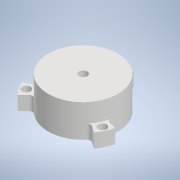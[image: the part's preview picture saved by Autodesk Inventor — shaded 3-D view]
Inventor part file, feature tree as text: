
AUTODESK INVENTOR PART (.ipt)
format: ipt  version: 2022 (Build 260153000, 153)  size: 250,368 bytes
history: native  units: in
note: dims shown in document units (in); Inventor stores cm internally (conversion verified against a paired STEP export)
features: extrude x5, sketch x5, projected_geometry x3, reference x3, other x3, fillet x2, chamfer x1
ambient origin geometry x8: Origin, YZ Plane, XZ Plane, XY Plane, X Axis, Y Axis, Z Axis, Center Point
bodies: Solid1 (feature_tree)
feature tree (22):
  extrude  "Extrusion1"  Depth=0.1181in
  extrude  "Extrusion3"  Depth=0.1181in
  extrude  "Extrusion4"  Depth=0.0591in
  extrude  "Extrusion5"  Depth=0.05in
  fillet  "Fillet1"  Radius=0.15in
  extrude  "Extrusion6"  Depth=0.15in
  fillet  "Fillet2"  Radius=0.0787in
  chamfer  "Chamfer2"  Distance=0.075in
  sketch  "Sketch1"  dims[d0=0.1181in d1=1.0in]
  sketch  "Sketch3"  dims[d2=0.1181in d3=0.0in d14=0.875in]
  sketch  "Sketch4"  dims[d15=0.3487in d16=0.0in d17=0.0591in]
  projected_geometry  "Projected Loop2"
  projected_geometry  "Projected Loop3"
  sketch  "Sketch5"  dims[d18=0.3in d19=0.05in d20=0.15in]
  projected_geometry  "Projected Loop4"
  sketch  "Sketch8"  dims[d21=0.05in d22=0.15in d23=0.0787in d24=0.0in d28=0.075in d29=45.0deg d30=135.0deg d31=7.874in d33=360.0deg d35=0.0787in d36=0.0in d37=0.275in d38=0.05in d39=0.15in d40=0.05in d41=135.0deg d42=0.05in d43=0.2in d44=0.0in d45=0.05in d46=0.1in d47=0.125in d48=45.0deg]
  reference  "Reference5"
  reference  "Reference6"
  reference  "Reference7"
  parser-record x1  (decoder bookkeeping rows leaked as tree rows — omitted from the tree; the rows remain in map.json)
  other  "Assembly1.iam"
  other  "CubeKnob:1"
note: 1 file-system path scrubbed to <path> (originals preserved in map.json)
